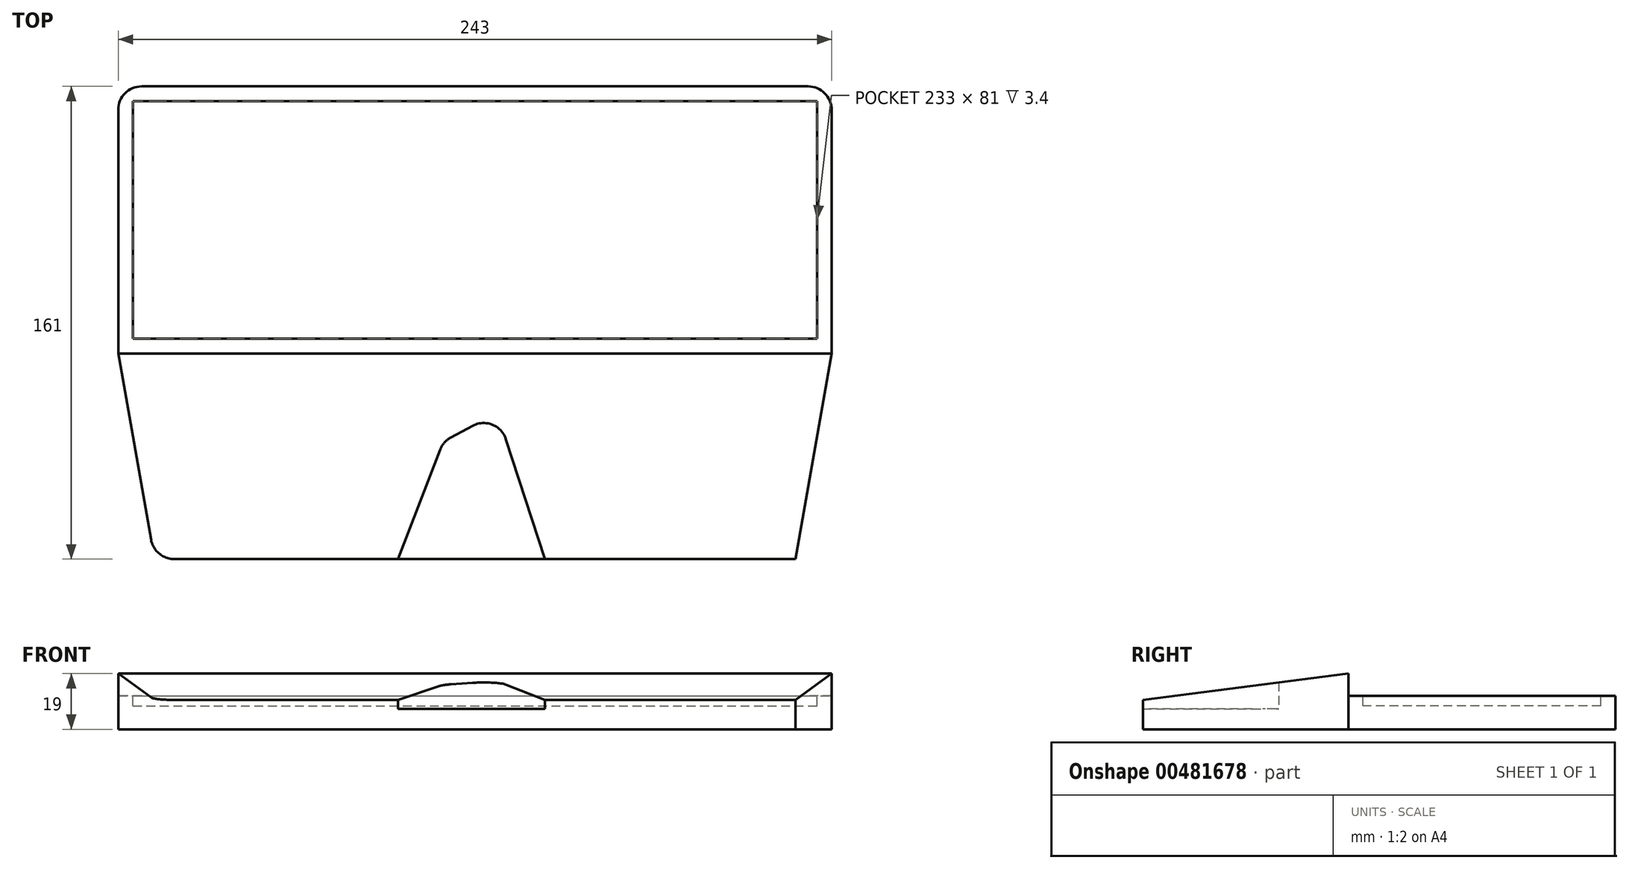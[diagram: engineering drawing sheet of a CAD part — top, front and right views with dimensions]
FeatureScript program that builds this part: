
annotation { "Feature Type Name" : "Feature", "Feature Type Description" : "" }
export const myFeature = defineFeature(function(context is Context, id is Id, definition is map)
    precondition{}
    {
        {
            var Q0;
            Q0=qCreatedBy(makeId("Top.planeOp"),FACE);
            var sketch = newSketch(context, id + "F0", { "sketchPlane" : qUnion([Q0])});
            skLineSegment(sketch, "E0.bottom", {"start": v(0, 0) * mm, "end": v(243, 0) * mm});
            skLineSegment(sketch, "E0.top", {"start": v(0, 161) * mm, "end": v(243, 161) * mm});
            skLineSegment(sketch, "E0.left", {"start": v(0, 0) * mm, "end": v(0, 161) * mm});
            skLineSegment(sketch, "E0.right", {"start": v(243, 0) * mm, "end": v(243, 161) * mm});
            skSolve(sketch);
        }
        {
            var Q0;
            Q0 = qSketchRegion(id + "F0", true);
            extrude(context, id + "F1", {"entities" : qUnion([Q0]), "depth" : 19 * mm});
        }
        {
            var Q0;
            Q0=makeQuery(id+"F1.opExtrude","CAP_FACE",FACE,{"disambiguationData":[OSD([sQuery(id+"F0.wireOp",EDGE,"E0.bottom"),sQuery(id+"F0.wireOp",EDGE,"E0.top"),sQuery(id+"F0.wireOp",EDGE,"E0.left"),sQuery(id+"F0.wireOp",EDGE,"E0.right")])],"isStart":false});
            var sketch = newSketch(context, id + "F2", { "sketchPlane" : qUnion([Q0])});
            skLineSegment(sketch, "E1.bottom", {"start": v(0, 161) * mm, "end": v(243, 161) * mm});
            skLineSegment(sketch, "E1.top", {"start": v(0, 70) * mm, "end": v(243, 70) * mm});
            skLineSegment(sketch, "E1.left", {"start": v(0, 161) * mm, "end": v(0, 70) * mm});
            skLineSegment(sketch, "E1.right", {"start": v(243, 161) * mm, "end": v(243, 70) * mm});
            skSolve(sketch);
        }
        {
            var Q0;
            Q0 = qSketchRegion(id + "F2", true);
            extrude(context, id + "F3", {"entities" : qUnion([Q0]), "operationType" : NewBodyOperationType.REMOVE, "oppositeDirection" : true, "depth" : 7.6 * mm});
        }
        {
            var Q0;
            Q0=makeQuery(id+"F3.boolean.opBoolean","COPY",FACE,{"derivedFrom":makeQuery(id+"F3.opExtrude","CAP_FACE",FACE,{"disambiguationData":[OSD([sQuery(id+"F2.wireOp",EDGE,"E1.bottom"),sQuery(id+"F2.wireOp",EDGE,"E1.top"),sQuery(id+"F2.wireOp",EDGE,"E1.left"),sQuery(id+"F2.wireOp",EDGE,"E1.right")])],"isStart":false})});
            var sketch = newSketch(context, id + "F4", { "sketchPlane" : qUnion([Q0])});
            skLineSegment(sketch, "E2.bottom", {"start": v(5, 156) * mm, "end": v(238, 156) * mm});
            skLineSegment(sketch, "E2.top", {"start": v(5, 75) * mm, "end": v(238, 75) * mm});
            skLineSegment(sketch, "E2.left", {"start": v(5, 156) * mm, "end": v(5, 75) * mm});
            skLineSegment(sketch, "E2.right", {"start": v(238, 156) * mm, "end": v(238, 75) * mm});
            skSolve(sketch);
        }
        {
            var Q0;
            Q0 = qSketchRegion(id + "F4", true);
            extrude(context, id + "F5", {"entities" : qUnion([Q0]), "operationType" : NewBodyOperationType.REMOVE, "oppositeDirection" : true, "depth" : 3.4 * mm});
        }
        {
            var Q0;
            Q0=makeQuery(id+"F1.opExtrude","CAP_FACE",FACE,{"disambiguationData":[OSD([sQuery(id+"F0.wireOp",EDGE,"E0.bottom"),sQuery(id+"F0.wireOp",EDGE,"E0.top"),sQuery(id+"F0.wireOp",EDGE,"E0.left"),sQuery(id+"F0.wireOp",EDGE,"E0.right")])],"isStart":false});
            var sketch = newSketch(context, id + "F6", { "sketchPlane" : qUnion([Q0])});
            skLineSegment(sketch, "E3", {"start": v(0, 70) * mm, "end": v(12.34, 0) * mm});
            skLineSegment(sketch, "E4", {"start": v(12.34, 0) * mm, "end": v(95.34, 0) * mm, "construction": true});
            skLineSegment(sketch, "E5", {"start": v(95.34, 0) * mm, "end": v(110.7, 40) * mm});
            skLineSegment(sketch, "E6", {"start": v(110.7, 40) * mm, "end": v(129.12, 49.93) * mm});
            skLineSegment(sketch, "E7", {"start": v(129.12, 49.93) * mm, "end": v(145.34, 0) * mm});
            skLineSegment(sketch, "E8", {"start": v(145.34, 0) * mm, "end": v(230.66, 0) * mm, "construction": true});
            skLineSegment(sketch, "E9", {"start": v(230.66, 0) * mm, "end": v(243, 70) * mm});
            skLineSegment(sketch, "E10", {"start": v(243, 70) * mm, "end": v(0, 70) * mm, "construction": true});
            skLineSegment(sketch, "E11", {"start": v(0, 70) * mm, "end": v(0, 0) * mm});
            skLineSegment(sketch, "E12", {"start": v(0, 0) * mm, "end": v(12.34, 0) * mm});
            skLineSegment(sketch, "E13", {"start": v(95.34, 0) * mm, "end": v(145.34, 0) * mm});
            skLineSegment(sketch, "E14", {"start": v(230.66, 0) * mm, "end": v(243, 0) * mm});
            skLineSegment(sketch, "E15", {"start": v(243, 0) * mm, "end": v(243, 70) * mm});
            skSolve(sketch);
        }
        {
            var Q0;
            Q0 = qSketchRegion(id + "F6", true);
            extrude(context, id + "F7", {"entities" : qUnion([Q0]), "operationType" : NewBodyOperationType.REMOVE, "endBound" : BoundingType.UP_TO_NEXT, "oppositeDirection" : true, "depth" : 25 * mm});
        }
        {
            var Q0;
            Q0=makeQuery(id+"F1.opExtrude","CAP_FACE",FACE,{"disambiguationData":[OSD([sQuery(id+"F0.wireOp",EDGE,"E0.bottom"),sQuery(id+"F0.wireOp",EDGE,"E0.top"),sQuery(id+"F0.wireOp",EDGE,"E0.left"),sQuery(id+"F0.wireOp",EDGE,"E0.right")])],"isStart":true});
            var sketch = newSketch(context, id + "F8", { "sketchPlane" : qUnion([Q0])});
            skLineSegment(sketch, "E16", {"start": v(95.34, 0) * mm, "end": v(145.34, 0) * mm});
            skLineSegment(sketch, "E17", {"start": v(145.34, 0) * mm, "end": v(129.12, -49.93) * mm});
            skLineSegment(sketch, "E18", {"start": v(129.12, -49.93) * mm, "end": v(110.7, -40) * mm});
            skLineSegment(sketch, "E19", {"start": v(110.7, -40) * mm, "end": v(95.34, 0) * mm});
            skSolve(sketch);
        }
        {
            var Q0;
            Q0 = qSketchRegion(id + "F8", true);
            extrude(context, id + "F9", {"entities" : qUnion([Q0]), "operationType" : NewBodyOperationType.ADD, "oppositeDirection" : true, "depth" : 7 * mm});
        }
        {
            var Q0;
            Q0=makeQuery(id+"F1.opExtrude","SWEPT_EDGE",EDGE,{"disambiguationData":[OSD([sQuery(id+"F0.wireOp",EDGE,"E0.top"),sQuery(id+"F0.wireOp",EDGE,"E0.left")])]});
            var Q1;
            Q1=makeQuery(id+"F1.opExtrude","SWEPT_EDGE",EDGE,{"disambiguationData":[OSD([sQuery(id+"F0.wireOp",EDGE,"E0.top"),sQuery(id+"F0.wireOp",EDGE,"E0.right")])]});
            var Q2;
            Q2=makeQuery(id+"F7.boolean.opBoolean","COPY",EDGE,{"derivedFrom":makeQuery(id+"F7.opExtrude","SWEPT_EDGE",EDGE,{"disambiguationData":[OSD([sQuery(id+"F0.wireOp",EDGE,"E0.bottom"),sQuery(id+"F6.wireOp",EDGE,"E9"),sQuery(id+"F6.wireOp",EDGE,"E14")])]})});
            var Q3;
            Q3=makeQuery(id+"F7.boolean.opBoolean","COPY",EDGE,{"derivedFrom":makeQuery(id+"F7.opExtrude","SWEPT_EDGE",EDGE,{"disambiguationData":[OSD([sQuery(id+"F0.wireOp",EDGE,"E0.bottom"),sQuery(id+"F6.wireOp",EDGE,"E3"),sQuery(id+"F6.wireOp",EDGE,"E12")])]})});
            var Q4;
            Q4=makeQuery(id+"F7.boolean.opBoolean","COPY",EDGE,{"derivedFrom":makeQuery(id+"F7.opExtrude","SWEPT_EDGE",EDGE,{"disambiguationData":[OSD([sQuery(id+"F6.wireOp",EDGE,"E5"),sQuery(id+"F6.wireOp",EDGE,"E6")])]})});
            var Q5;
            Q5=makeQuery(id+"F7.boolean.opBoolean","COPY",EDGE,{"derivedFrom":makeQuery(id+"F7.opExtrude","SWEPT_EDGE",EDGE,{"disambiguationData":[OSD([sQuery(id+"F6.wireOp",EDGE,"E6"),sQuery(id+"F6.wireOp",EDGE,"E7")])]})});
            fillet(context, id + "F10", {"entities" : qUnion([Q0, Q1, Q2, Q3, Q4, Q5]), "radius" : 8 * mm, "tangentPropagation" : true, "allowEdgeOverflow" : false});
        }
        {
            var Q0;
            Q0=makeQuery(id+"F1.opExtrude","SWEPT_FACE",FACE,{"disambiguationData":[OSD([sQuery(id+"F0.wireOp",EDGE,"E0.right")])]});
            var sketch = newSketch(context, id + "F11", { "sketchPlane" : qUnion([Q0])});
            skLineSegment(sketch, "E20", {"start": v(0, 10) * mm, "end": v(70, 19) * mm});
            skLineSegment(sketch, "E21", {"start": v(70, 19) * mm, "end": v(0, 19) * mm});
            skLineSegment(sketch, "E22", {"start": v(0, 19) * mm, "end": v(0, 10) * mm});
            skSolve(sketch);
        }
        {
            var Q0;
            Q0 = qSketchRegion(id + "F11", true);
            var Q1;
            Q1=makeQuery(id+"F1.opExtrude","SWEPT_FACE",FACE,{"disambiguationData":[OSD([sQuery(id+"F0.wireOp",EDGE,"E0.left")])]});
            extrude(context, id + "F12", {"entities" : qUnion([Q0]), "operationType" : NewBodyOperationType.REMOVE, "endBound" : BoundingType.UP_TO_SURFACE, "oppositeDirection" : true, "endBoundEntityFace" : qUnion([Q1]), "depth" : 25 * mm});
        }
    });
